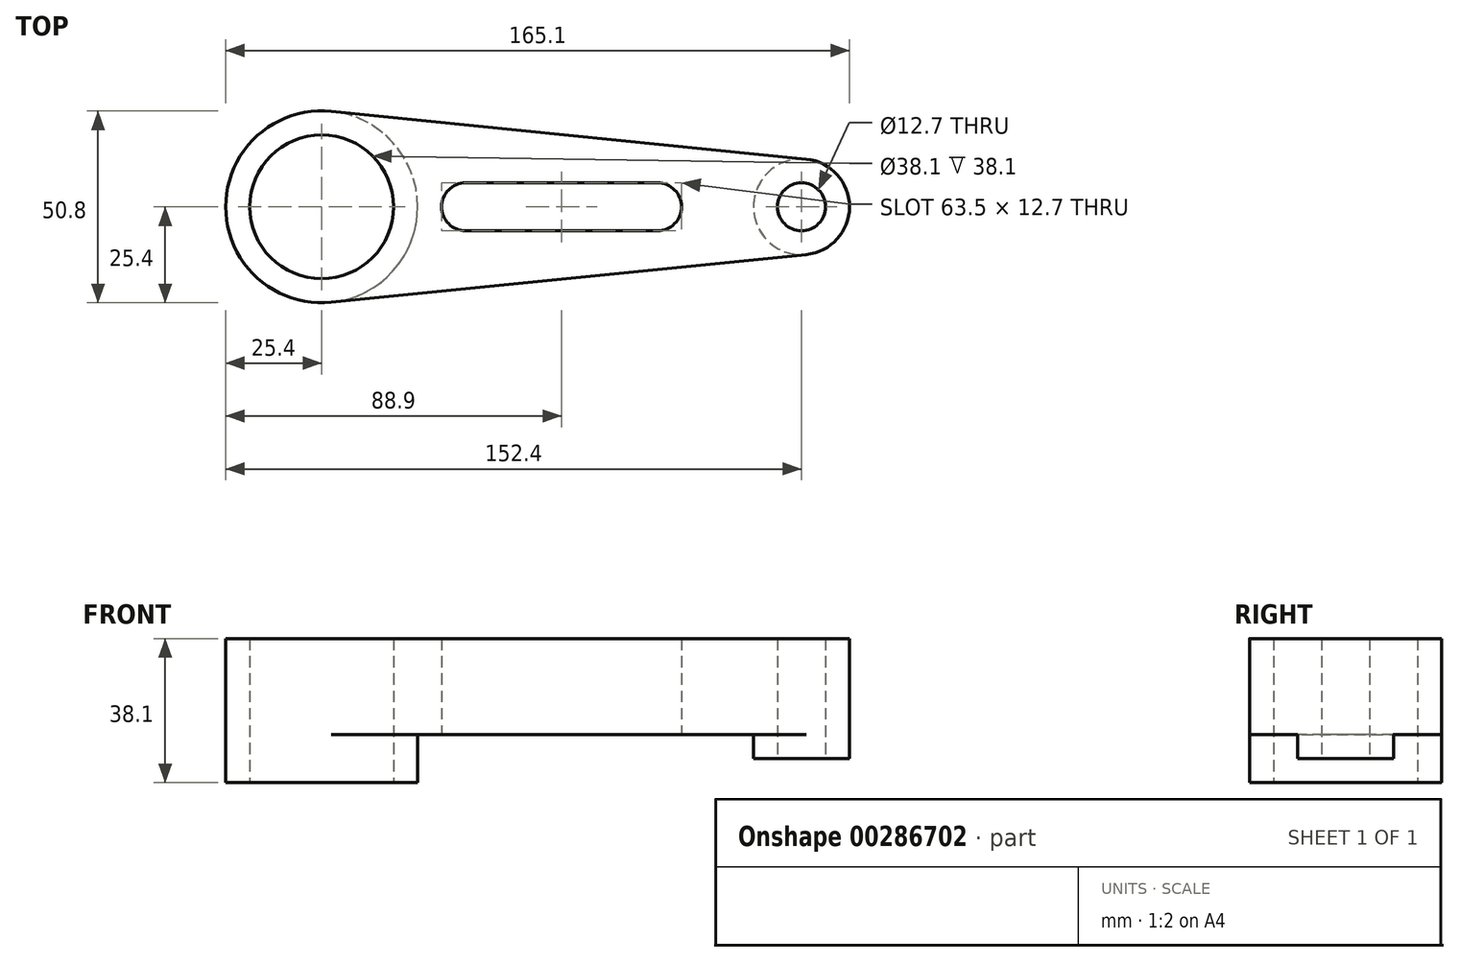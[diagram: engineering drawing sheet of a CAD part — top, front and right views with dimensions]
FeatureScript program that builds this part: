
annotation { "Feature Type Name" : "Feature", "Feature Type Description" : "" }
export const myFeature = defineFeature(function(context is Context, id is Id, definition is map)
    precondition{}
    {
        {
            var Q0;
            Q0=qCreatedBy(makeId("Top.planeOp"),FACE);
            var sketch = newSketch(context, id + "F0", { "sketchPlane" : qUnion([Q0])});
            skCircle(sketch, "E0", {"center": v(0, 0) * mm, "radius": 25.4 * mm});
            skCircle(sketch, "E1", {"center": v(0, 0) * mm, "radius": 19.05 * mm});
            skArc(sketch, "E2", {"start": v(38.1, 6.35) * mm, "mid": v(31.75, 0) * mm, "end": v(38.1, -6.35) * mm});
            skArc(sketch, "E3", {"start": v(88.9, -6.35) * mm, "mid": v(95.25, 0) * mm, "end": v(88.9, 6.35) * mm});
            skCircle(sketch, "E4", {"center": v(127, 0) * mm, "radius": 6.35 * mm});
            skCircle(sketch, "E5", {"center": v(127, 0) * mm, "radius": 12.7 * mm});
            skLineSegment(sketch, "E6", {"start": v(38.1, 6.35) * mm, "end": v(88.9, 6.35) * mm});
            skLineSegment(sketch, "E7", {"start": v(38.1, -6.35) * mm, "end": v(88.9, -6.35) * mm});
            skLineSegment(sketch, "E8", {"start": v(2.54, 25.27) * mm, "end": v(128.27, 12.64) * mm});
            skLineSegment(sketch, "E9", {"start": v(2.54, -25.27) * mm, "end": v(128.27, -12.64) * mm});
            skSolve(sketch);
        }
        {
            var Q0;
            Q0 = qSketchRegion(id + "F0", true);
            extrude(context, id + "F1", {"entities" : qUnion([Q0]), "depth" : 25.4 * mm});
        }
        {
            var Q0;
            Q0=makeQuery(id+"F0.imprint","IMPRINT",FACE,{"disambiguationData":[TD([[makeQuery(id+"F0.imprint","IMPRINT",EDGE,{"derivedFrom":sQuery(id+"F0.wireOp",EDGE,"E4")}),-1.0]])]});
            extrude(context, id + "F2", {"entities" : qUnion([Q0]), "operationType" : NewBodyOperationType.ADD, "oppositeDirection" : true, "depth" : 6.35 * mm});
        }
        {
            var Q0;
            Q0=makeQuery(id+"F0.imprint","IMPRINT",FACE,{"disambiguationData":[TD([[makeQuery(id+"F0.imprint","IMPRINT",EDGE,{"derivedFrom":sQuery(id+"F0.wireOp",EDGE,"E1")}),-1.0]])]});
            extrude(context, id + "F3", {"entities" : qUnion([Q0]), "operationType" : NewBodyOperationType.ADD, "oppositeDirection" : true, "depth" : 12.7 * mm});
        }
    });
